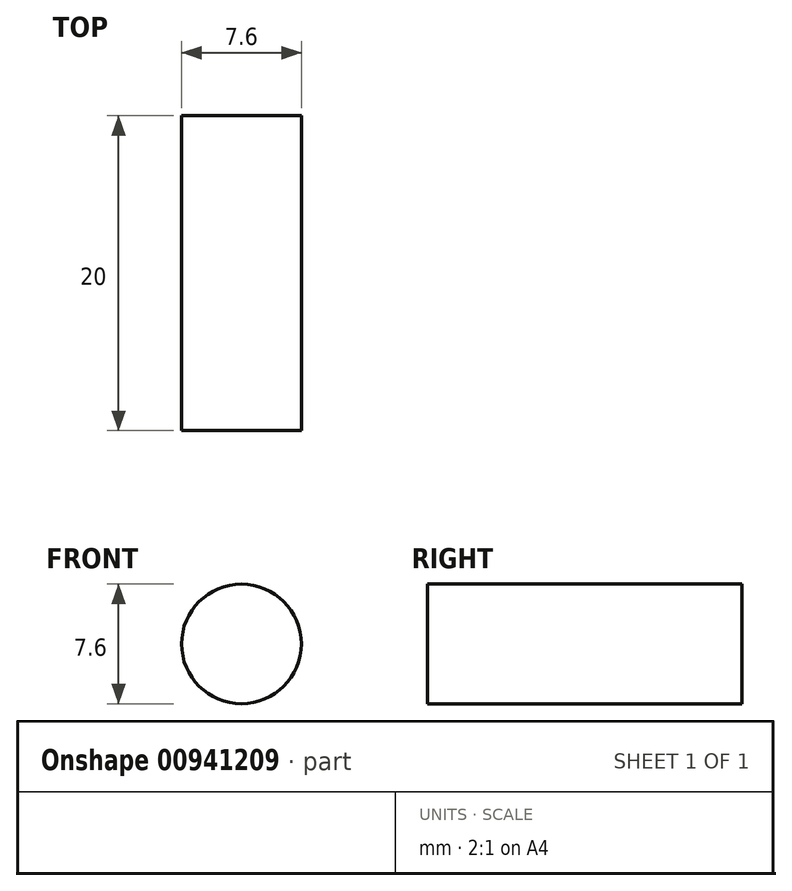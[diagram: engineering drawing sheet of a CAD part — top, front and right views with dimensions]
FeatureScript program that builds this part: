
annotation { "Feature Type Name" : "Feature", "Feature Type Description" : "" }
export const myFeature = defineFeature(function(context is Context, id is Id, definition is map)
    precondition{}
    {
        {
            var Q0;
            Q0=qCreatedBy(makeId("Front.planeOp"),FACE);
            var sketch = newSketch(context, id + "F0", { "sketchPlane" : qUnion([Q0])});
            skCircle(sketch, "E0", {"center": v(0, 0) * mm, "radius": 3.8 * mm});
            skSolve(sketch);
        }
        {
            var Q0;
            Q0 = qSketchRegion(id + "F0", true);
            extrude(context, id + "F1", {"entities" : qUnion([Q0]), "depth" : 20 * mm, "offsetDistance" : 25 * mm});
        }
    });
